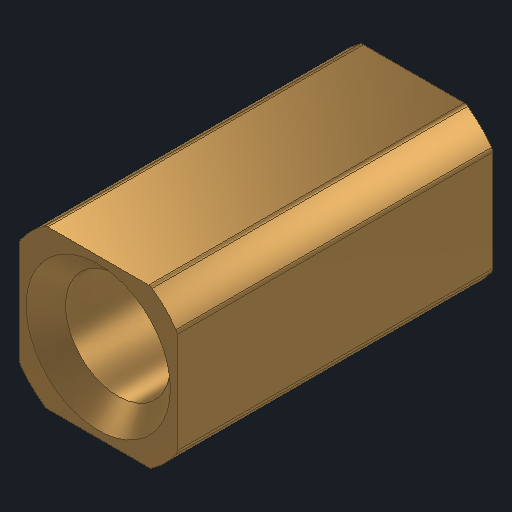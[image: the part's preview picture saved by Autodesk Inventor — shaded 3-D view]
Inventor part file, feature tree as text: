
AUTODESK INVENTOR PART (.ipt)
format: ipt  version: 2024 (Build 280153000, 153)  size: 176,128 bytes
history: native  units: in
note: dims shown in document units (in); Inventor stores cm internally (conversion verified against a paired STEP export)
features: extrude x2, fillet x1, chamfer x1
ambient origin geometry x8: Origin, YZ Plane, XZ Plane, XY Plane, X Axis, Y Axis, Z Axis, Center Point
bodies: Solid1 (feature_tree)
feature tree (4):
  extrude  "Extrusion1"  Depth=0.3in
  extrude  "Extrusion2"  Depth=0.25in
  fillet  "Fillet1"  Radius=0.5in
  chamfer  "Chamfer1"  Distance=0.166in
